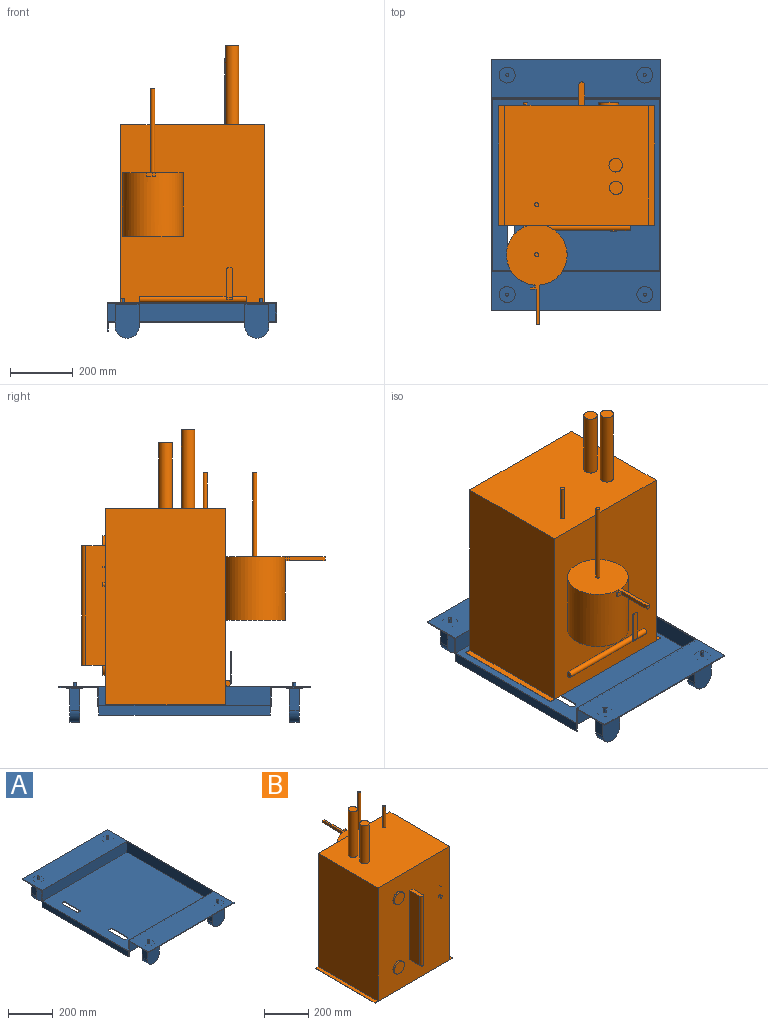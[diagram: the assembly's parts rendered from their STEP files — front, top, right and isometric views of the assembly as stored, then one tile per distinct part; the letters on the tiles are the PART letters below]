
ASSEMBLY  parts=2 mates=2
PART A: 94 faces, bbox 539.8x800.1x126.7 mm
  f0: plane 552.45x539.75mm, normal (0,0,-1), area 292185.6mm2, adj f5,f6,f8,f9,f10,f11,f12,f13
  f1: plane 39.66x9.53mm, normal (0,0,-1), area 263.1mm2, adj f54,f85
  f2: plane 39.66x9.53mm, normal (0,0,-1), area 263.1mm2, adj f49,f78
  f3: plane 39.66x9.53mm, normal (0,0,-1), area 263.1mm2, adj f44,f71
  f4: plane 39.66x9.53mm, normal (0,0,-1), area 263.1mm2, adj f39,f61
  f5: plane 539.75x58.74mm, normal (0,-1,0), area 31703.6mm2, adj f0,f8,f9,f34
  f6: plane 539.75x58.74mm, normal (0,1,0), area 31703.6mm2, adj f0,f8,f9,f33
  f7: plane 546.1x536.58mm, normal (0,0,1), area 288758.2mm2, adj f8,f10,f11,f12,f13,f14,f15,f16
  f8: plane 800.1x90.49mm, normal (-1,0,0), area 18518.1mm2, adj f0,f5,f6,f7,f26,f27,f29,f30
  f9: plane 800.1x61.91mm, normal (1,0,0), area 34989.8mm2, adj f0,f5,f6,f29,f30,f33,f34,f35
  f10: plane 6.35x3.18mm, normal (0,1,0), area 20.2mm2, adj f0,f7,f11,f24
  f11: cylinder r=6.35mm len=6.35mm, axis (0,0,-1), area 31.7mm2, adj f0,f7,f10,f12
  f12: plane 88.9x3.18mm, normal (1,0,0), area 282.3mm2, adj f0,f7,f11,f13
  f13: cylinder r=6.35mm len=6.35mm, axis (0,0,-1), area 31.7mm2, adj f0,f7,f12,f14
  f14: plane 6.35x3.18mm, normal (0,-1,0), area 20.2mm2, adj f0,f7,f13,f15
  f15: cylinder r=6.35mm len=6.35mm, axis (0,0,-1), area 31.7mm2, adj f0,f7,f14,f16
  f16: plane 88.9x3.18mm, normal (-1,0,0), area 282.3mm2, adj f0,f7,f15,f24
  f17: plane 9.53x3.18mm, normal (0,1,0), area 30.2mm2, adj f0,f7,f18,f25
  f18: cylinder r=6.35mm len=6.35mm, axis (0,0,-1), area 31.7mm2, adj f0,f7,f17,f19
  f19: plane 95.25x3.18mm, normal (1,0,0), area 302.4mm2, adj f0,f7,f18,f20
  f20: cylinder r=6.35mm len=6.35mm, axis (0,0,-1), area 31.7mm2, adj f0,f7,f19,f21
  f21: plane 9.53x3.18mm, normal (0,-1,0), area 30.2mm2, adj f0,f7,f20,f22
  f22: cylinder r=6.35mm len=6.35mm, axis (0,0,-1), area 31.7mm2, adj f0,f7,f21,f23
  f23: plane 95.25x3.18mm, normal (-1,0,0), area 302.4mm2, adj f0,f7,f22,f25
  f24: cylinder r=6.35mm len=6.35mm, axis (0,0,-1), area 31.7mm2, adj f0,f7,f10,f16
  f25: cylinder r=6.35mm len=6.35mm, axis (0,0,-1), area 31.7mm2, adj f0,f7,f17,f23
  f26: plane 536.58x58.74mm, normal (0,1,0), area 31517.1mm2, adj f7,f8,f28,f29
  f27: plane 536.58x58.74mm, normal (0,-1,0), area 31517.1mm2, adj f7,f8,f28,f29
  f28: plane 546.1x58.74mm, normal (-1,0,0), area 32076.5mm2, adj f7,f26,f27,f29
  f29: plane 800.1x539.75mm, normal (0,0,1), area 138545.3mm2, adj f8,f9,f26,f27,f28,f30,f31,f32
  f30: plane 539.75x3.18mm, normal (0,1,0), area 1713.7mm2, adj f8,f9,f29,f33
  f31: cylinder r=4.76mm len=9.53mm, axis (0,0,1), area 95mm2, adj f29,f55
  f32: cylinder r=4.76mm len=9.53mm, axis (0,0,1), area 95mm2, adj f29,f50
  f33: plane 539.75x123.83mm, normal (0,0,-1), area 62780.9mm2, adj f6,f8,f9,f30,f49,f54
  f34: plane 539.75x123.83mm, normal (0,0,-1), area 62780.9mm2, adj f5,f8,f9,f35,f39,f44
  f35: plane 539.75x3.18mm, normal (0,-1,0), area 1713.7mm2, adj f8,f9,f29,f34
  f36: cylinder r=4.76mm len=9.53mm, axis (0,0,1), area 95mm2, adj f29,f45
  f37: cylinder r=4.76mm len=9.53mm, axis (0,0,1), area 95mm2, adj f29,f40
  f38: plane 39.66x9.53mm, normal (0,0,-1), area 263.1mm2, adj f39,f63
  f39: cylinder r=25.4mm len=50.8mm, axis (0,0,1), area 263.5mm2, adj f4,f34,f38,f58,f59,f60
  f40: plane 9.53x9.53mm, normal (0,0,1), area 1.9mm2, adj f37,f41
  f41: cylinder r=4.7mm len=17.15mm, axis (0,0,-1), area 506.2mm2, adj f40,f42
  f42: plane 9.4x9.4mm, normal (0,0,1), area 69.4mm2, adj f41
  f43: plane 39.66x9.53mm, normal (0,0,-1), area 263.1mm2, adj f44,f69
  f44: cylinder r=25.4mm len=50.8mm, axis (0,0,1), area 263.5mm2, adj f3,f34,f43,f65,f66,f67
  f45: plane 9.53x9.53mm, normal (0,0,1), area 1.9mm2, adj f36,f46
  f46: cylinder r=4.7mm len=17.15mm, axis (0,0,-1), area 506.2mm2, adj f45,f47
  f47: plane 9.4x9.4mm, normal (0,0,1), area 69.4mm2, adj f46
  f48: plane 39.66x9.53mm, normal (0,0,-1), area 263.1mm2, adj f49,f76
  f49: cylinder r=25.4mm len=50.8mm, axis (0,0,1), area 263.5mm2, adj f2,f33,f48,f72,f73,f74
  f50: plane 9.53x9.53mm, normal (0,0,1), area 1.9mm2, adj f32,f51
  f51: cylinder r=4.7mm len=17.15mm, axis (0,0,-1), area 506.2mm2, adj f50,f52
  f52: plane 9.4x9.4mm, normal (0,0,1), area 69.4mm2, adj f51
  f53: plane 39.66x9.53mm, normal (0,0,-1), area 263.1mm2, adj f54,f83
  f54: cylinder r=25.4mm len=50.8mm, axis (0,0,1), area 263.5mm2, adj f1,f33,f53,f79,f80,f81
  f55: plane 9.53x9.53mm, normal (0,0,1), area 1.9mm2, adj f31,f56
  f56: cylinder r=4.7mm len=17.15mm, axis (0,0,-1), area 506.2mm2, adj f55,f57
  f57: plane 9.4x9.4mm, normal (0,0,1), area 69.4mm2, adj f56
  f58: plane 15.88x5.57mm, normal (0,0,1), area 28.1mm2, adj f39,f61,f62
  f59: plane 15.88x5.57mm, normal (0,0,1), area 28.1mm2, adj f39,f62,f63
  f60: plane 31.75x30.97mm, normal (0,0,1), area 862.6mm2, adj f39,f61,f63,f64
  f61: plane 107.89x76.2mm, normal (0,-1,0), area 7597.9mm2, adj f4,f58,f60,f62,f64,f86
  f62: plane 69.79x31.75mm, normal (-1,0,0), area 2215.7mm2, adj f58,f59,f61,f63,f86
  f63: plane 107.89x76.2mm, normal (0,1,0), area 7597.9mm2, adj f38,f59,f60,f62,f64,f86
  f64: plane 69.79x31.75mm, normal (1,0,0), area 2215.7mm2, adj f60,f61,f63,f86
  f65: plane 31.75x30.97mm, normal (0,0,1), area 862.6mm2, adj f44,f68,f69,f71
  f66: plane 15.88x5.57mm, normal (0,0,1), area 28.1mm2, adj f44,f70,f71
  f67: plane 15.88x5.57mm, normal (0,0,1), area 28.1mm2, adj f44,f69,f70
  f68: plane 69.79x31.75mm, normal (-1,0,0), area 2215.7mm2, adj f65,f69,f71,f89
  f69: plane 107.89x76.2mm, normal (0,1,0), area 7597.9mm2, adj f43,f65,f67,f68,f70,f89
  f70: plane 69.79x31.75mm, normal (1,0,0), area 2215.7mm2, adj f66,f67,f69,f71,f89
  f71: plane 107.89x76.2mm, normal (0,-1,0), area 7597.9mm2, adj f3,f65,f66,f68,f70,f89
  f72: plane 15.88x5.57mm, normal (0,0,1), area 28.1mm2, adj f49,f75,f78
  f73: plane 15.88x5.57mm, normal (0,0,1), area 28.1mm2, adj f49,f75,f76
  f74: plane 31.75x30.97mm, normal (0,0,1), area 862.6mm2, adj f49,f76,f77,f78
  f75: plane 69.79x31.75mm, normal (-1,0,0), area 2215.7mm2, adj f72,f73,f76,f78,f88
  f76: plane 107.89x76.2mm, normal (0,1,0), area 7597.9mm2, adj f48,f73,f74,f75,f77,f88
  f77: plane 69.79x31.75mm, normal (1,0,0), area 2215.7mm2, adj f74,f76,f78,f88
  f78: plane 107.89x76.2mm, normal (0,-1,0), area 7597.9mm2, adj f2,f72,f74,f75,f77,f88
  f79: plane 31.75x30.97mm, normal (0,0,1), area 862.6mm2, adj f54,f82,f83,f85
  f80: plane 15.88x5.57mm, normal (0,0,1), area 28.1mm2, adj f54,f84,f85
  f81: plane 15.88x5.57mm, normal (0,0,1), area 28.1mm2, adj f54,f83,f84
  f82: plane 69.79x31.75mm, normal (-1,0,0), area 2215.7mm2, adj f79,f83,f85,f87
  f83: plane 107.89x76.2mm, normal (0,1,0), area 7597.9mm2, adj f53,f79,f81,f82,f84,f87
  f84: plane 69.79x31.75mm, normal (1,0,0), area 2215.7mm2, adj f80,f81,f83,f85,f87
  f85: plane 107.89x76.2mm, normal (0,-1,0), area 7597.9mm2, adj f1,f79,f80,f82,f84,f87
  f86: cylinder r=38.1mm len=76.2mm, axis (0,1,0), area 3800.3mm2, adj f61,f62,f63,f64
  f87: cylinder r=38.1mm len=76.2mm, axis (0,-1,0), area 3800.3mm2, adj f82,f83,f84,f85
  f88: cylinder r=38.1mm len=76.2mm, axis (0,-1,0), area 3800.3mm2, adj f75,f76,f77,f78
  f89: cylinder r=38.1mm len=76.2mm, axis (0,-1,0), area 3800.3mm2, adj f68,f69,f70,f71
  f90: plane 546.1x28.58mm, normal (1,0,0), area 15604.8mm2, adj f0,f91,f92,f93
  f91: plane 28.58x3.18mm, normal (0,1,0), area 90.7mm2, adj f0,f8,f90,f93
  f92: plane 28.58x3.18mm, normal (0,-1,0), area 90.7mm2, adj f0,f8,f90,f93
  f93: plane 546.1x3.18mm, normal (0,0,-1), area 1733.9mm2, adj f8,f90,f91,f92
PART B: 54 faces, bbox 495.3x774x876.3 mm
  f0: cylinder r=9.53mm len=340.36mm, axis (-1,0,0), area 15427.6mm2, adj f2,f40,f41,f46,f47,f51,f52
  f1: plane 624.21x381mm, normal (-1,0,0), area 237822.1mm2, adj f2,f3,f6,f42
  f2: plane 625.48x495.3mm, normal (0,1,0), area 272667.8mm2, adj f0,f1,f4,f5,f6,f25,f26,f27
  f3: plane 625.48x495.3mm, normal (0,-1,0), area 272289.1mm2, adj f1,f4,f5,f6,f11,f13,f15,f17
  f4: plane 624.21x381mm, normal (1,0,0), area 237822.1mm2, adj f2,f3,f6,f44
  f5: plane 495.3x381mm, normal (0,0,-1), area 188709.3mm2, adj f2,f3,f43,f45
  f6: plane 457.2x381mm, normal (0,0,1), area 171229.3mm2, adj f1,f2,f3,f4,f7,f9,f38
  f7: cylinder r=21.09mm len=250.83mm, axis (0,0,-1), area 33243mm2, adj f6,f8
  f8: plane 42.19x42.19mm, normal (0,0,1), area 1397.8mm2, adj f7
  f9: cylinder r=21.4mm len=209.55mm, axis (0,0,-1), area 28182.4mm2, adj f6,f10
  f10: plane 42.81x42.81mm, normal (0,0,1), area 1439.4mm2, adj f9
  f11: cylinder r=31.75mm len=63.5mm, axis (0,1,0), area 1900.2mm2, adj f3,f12
  f12: plane 63.5x63.5mm, normal (0,-1,0), area 3166.9mm2, adj f11
  f13: cylinder r=31.75mm len=63.5mm, axis (0,1,0), area 1900.2mm2, adj f3,f14
  f14: plane 63.5x63.5mm, normal (0,-1,0), area 3166.9mm2, adj f13
  f15: cylinder r=1.59mm len=9.53mm, axis (0,1,0), area 95mm2, adj f3,f16
  f16: plane 3.18x3.18mm, normal (0,-1,0), area 7.9mm2, adj f15
  f17: cylinder r=6.35mm len=12.7mm, axis (0,1,0), area 380mm2, adj f3,f18
  f18: plane 12.7x12.7mm, normal (0,-1,0), area 126.7mm2, adj f17
  f19: plane 381x63.5mm, normal (-1,0,0), area 24193.5mm2, adj f3,f20,f22,f23
  f20: plane 75.8x19.05mm, normal (0,0,-1), area 1383.2mm2, adj f3,f19,f21,f23,f24
  f21: plane 381x63.5mm, normal (1,0,0), area 24193.5mm2, adj f3,f20,f22,f24
  f22: plane 75.8x19.05mm, normal (0,0,1), area 1383.2mm2, adj f3,f19,f21,f23,f24
  f23: cylinder r=12.7mm len=381mm, axis (0,0,1), area 6378mm2, adj f19,f20,f22,f24
  f24: cylinder r=12.7mm len=381mm, axis (0,0,-1), area 6378mm2, adj f20,f21,f22,f23
  f25: cylinder r=96.52mm len=203.2mm, axis (0,0,1), area 114051mm2, adj f2,f26,f27,f28,f34,f35
  f26: plane 193.04x190.5mm, normal (0,0,-1), area 29192.7mm2, adj f2,f25
  f27: plane 317.17x193.04mm, normal (0,0,1), area 30486.3mm2, adj f2,f25,f28,f29,f30,f31,f32,f33
  f28: plane 12.7x6.13mm, normal (1,0,0), area 77.9mm2, adj f25,f27,f29,f35
  f29: plane 15.88x12.7mm, normal (0,-1,0), area 201.6mm2, adj f27,f28,f30,f35
  f30: plane 12.7x6.35mm, normal (1,0,0), area 80.6mm2, adj f27,f29,f31,f35
  f31: plane 18.42x12.7mm, normal (0,1,0), area 233.9mm2, adj f27,f30,f32,f35
  f32: plane 114.3x12.7mm, normal (1,0,0), area 1451.6mm2, adj f27,f31,f33,f35
  f33: plane 12.7x10.16mm, normal (0,1,0), area 129mm2, adj f27,f32,f34,f35
  f34: plane 127x12.7mm, normal (-1,0,0), area 1612.9mm2, adj f25,f27,f33,f35
  f35: plane 127x28.58mm, normal (0,0,-1), area 1420.2mm2, adj f25,f28,f29,f30,f31,f32,f33,f34
  f36: cylinder r=6.35mm len=266.7mm, axis (0,0,-1), area 10640.9mm2, adj f27,f37
  f37: plane 12.7x12.7mm, normal (0,0,1), area 126.7mm2, adj f36
  f38: cylinder r=6.35mm len=114.3mm, axis (0,0,-1), area 4560.4mm2, adj f6,f39
  f39: plane 12.7x12.7mm, normal (0,0,1), area 126.7mm2, adj f38
  f40: plane 19.05x16.51mm, normal (1,0,0), area 262.4mm2, adj f0,f2
  f41: plane 19.05x16.51mm, normal (-1,0,0), area 262.4mm2, adj f0,f2
  f42: plane 381x19.05mm, normal (0,0,1), area 7258.1mm2, adj f1,f2,f3,f43
  f43: plane 381x1.27mm, normal (-1,0,0), area 483.9mm2, adj f2,f3,f5,f42
  f44: plane 381x19.05mm, normal (0,0,1), area 7258.1mm2, adj f2,f3,f4,f45
  f45: plane 381x1.27mm, normal (1,0,0), area 483.9mm2, adj f2,f3,f5,f44
  f46: plane 19.05x1.91mm, normal (0,0,-1), area 36.3mm2, adj f0,f51,f52,f53
  f47: plane 96.85x19.05mm, normal (0,-1,0), area 1827.6mm2, adj f0,f48,f49,f50,f51,f52
  f48: cylinder r=6.35mm len=6.35mm, axis (0,-1,0), area 31.7mm2, adj f47,f49,f52,f53
  f49: plane 6.35x3.18mm, normal (0,0,1), area 20.2mm2, adj f47,f48,f50,f53
  f50: cylinder r=6.35mm len=6.35mm, axis (0,-1,0), area 31.7mm2, adj f47,f49,f51,f53
  f51: plane 95.25x3.18mm, normal (-1,0,0), area 298.3mm2, adj f0,f46,f47,f50,f53
  f52: plane 95.25x3.18mm, normal (1,0,0), area 298.3mm2, adj f0,f46,f47,f48,f53
  f53: plane 101.6x19.05mm, normal (0,1,0), area 1918.2mm2, adj f46,f48,f49,f50,f51,f52
PLACE A t=(-91.25,-57.49,-19.75)mm fixed
PLACE B rot(axis=(0,0,1),180deg) t=(-88.96,3.57,608.9)mm
MATE parallel B.f4 <-> A.f8  axis (-1,0,0) through (-317.56,3.57,296.8)mm
MATE planar B.f5 <-> A.f7  axis (0,0,-1) through (-88.96,3.57,-16.57)mm
